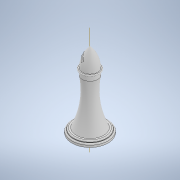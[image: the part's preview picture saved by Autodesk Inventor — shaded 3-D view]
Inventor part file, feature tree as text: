
AUTODESK INVENTOR PART (.ipt)
format: ipt  version: 2022 (Build 260153000, 153)  size: 242,176 bytes
history: native  units: mm
features: other x3, sketch x3, plane x2, extrude x2, revolve x1, fillet x1
ambient origin geometry x8: Origin, YZ Plane, XZ Plane, XY Plane, X Axis, Y Axis, Z Axis, Center Point
bodies: Solid1 (feature_tree)
feature tree (12):
  other  "Back Line Base.ipt"
  revolve  "Revolution1"  [1 undecoded]
  plane  "Work Plane2"
  extrude  "Extrusion1"  Depth=1.0mm
  extrude  "Extrusion2"  Depth=0.5mm
  fillet  "Fillet1"  Radius=12.0mm
  other  "Solid1::Back Line Base.ipt"
  other  "TaggingFeature1"
  sketch  "Sketch1"  dims[d0=10.0mm d1=45.0mm]
  plane  "Work Plane1"
  sketch  "Sketch2"  dims[d2=1.0mm d3=1.0mm]
  sketch  "Sketch3"  dims[d4=1.0mm d5=3.0mm d7=12.0mm d8=1.0mm d9=50.0mm d10=90.0deg d11=17.0mm d12=45.0deg d13=29.5mm d14=2.0mm d15=0.0mm d16=1.0mm d17=2.0mm d18=0.0mm d19=0.5mm]
note: 1 required parameter value undecoded (feature->parameter linkage not recoverable at this tier; creation-order binding heuristic only, values carry confidence <= 0.55)
